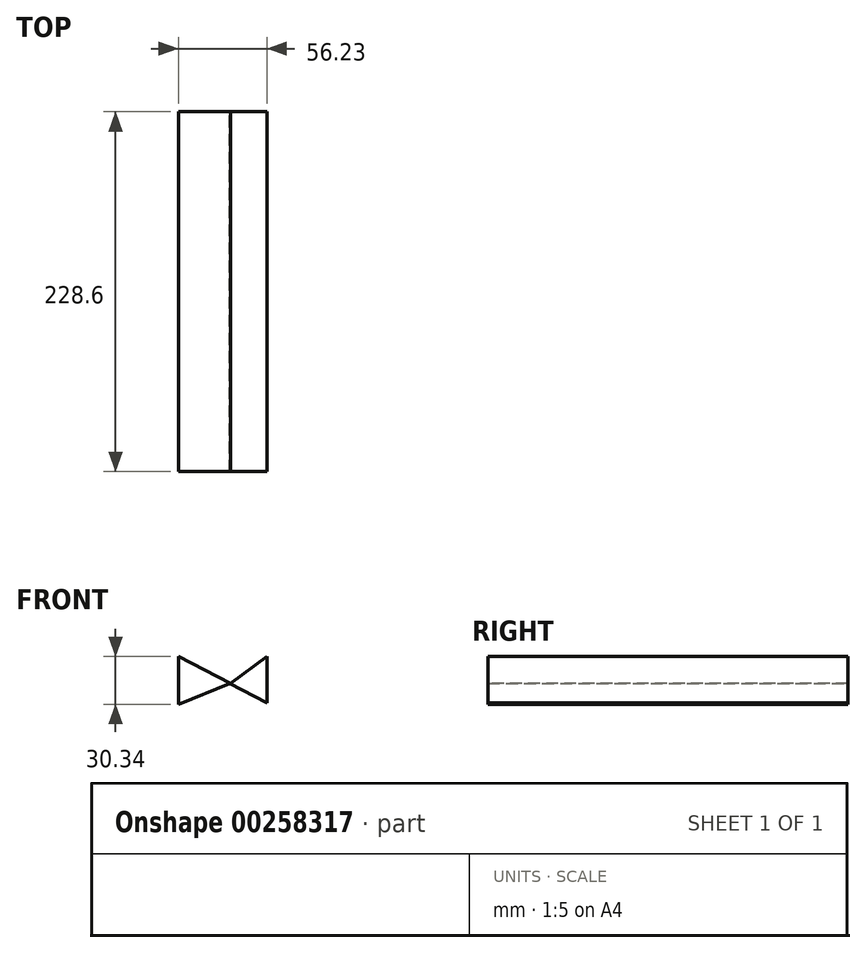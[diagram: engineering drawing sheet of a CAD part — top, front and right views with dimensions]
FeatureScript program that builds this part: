
annotation { "Feature Type Name" : "Feature", "Feature Type Description" : "" }
export const myFeature = defineFeature(function(context is Context, id is Id, definition is map)
    precondition{}
    {
        {
            var Q0;
            Q0=qCreatedBy(makeId("Front.planeOp"),FACE);
            var sketch = newSketch(context, id + "F0", { "sketchPlane" : qUnion([Q0])});
            skLineSegment(sketch, "E0", {"start": v(1.64, 0) * mm, "end": v(1.64, -34.8) * mm});
            skLineSegment(sketch, "E1", {"start": v(1.64, -34.8) * mm, "end": v(-30.22, -16.99) * mm});
            skLineSegment(sketch, "E2", {"start": v(-30.22, -16.99) * mm, "end": v(-63.26, -30.34) * mm});
            skLineSegment(sketch, "E3", {"start": v(-63.26, -30.34) * mm, "end": v(-63.26, 0) * mm});
            skLineSegment(sketch, "E4", {"start": v(-63.26, 0) * mm, "end": v(-30.22, -16.99) * mm});
            skLineSegment(sketch, "E5", {"start": v(-30.22, -16.99) * mm, "end": v(0, 0) * mm});
            skSolve(sketch);
        }
        {
            var Q0;
            Q0=makeQuery(id+"F0.imprint","IMPRINT",FACE,{"disambiguationData":[TD([[makeQuery(id+"F0.imprint","IMPRINT",EDGE,{"derivedFrom":sQuery(id+"F0.wireOp",EDGE,"E2")}),-1.0]])]});
            extrude(context, id + "F1", {"entities" : qUnion([Q0]), "depth" : 228.6 * mm});
        }
        {
            var Q0;
            Q0=qCreatedBy(makeId("Front.planeOp"),FACE);
            var sketch = newSketch(context, id + "F2", { "sketchPlane" : qUnion([Q0])});
            skLineSegment(sketch, "E6", {"start": v(-30.7, -17.22) * mm, "end": v(-7.03, 0) * mm});
            skLineSegment(sketch, "E7", {"start": v(-7.03, 0) * mm, "end": v(-7.03, -29.4) * mm});
            skLineSegment(sketch, "E8", {"start": v(-7.03, -29.4) * mm, "end": v(-30.7, -17.22) * mm});
            skSolve(sketch);
        }
        {
            var Q0;
            Q0=makeQuery(id+"F2.imprint","IMPRINT",FACE,{"disambiguationData":[TD([[makeQuery(id+"F2.imprint","IMPRINT",EDGE,{"derivedFrom":sQuery(id+"F2.wireOp",EDGE,"E6")}),-1.0]])]});
            extrude(context, id + "F3", {"entities" : qUnion([Q0]), "operationType" : NewBodyOperationType.ADD, "depth" : 228.6 * mm});
        }
    });
